# Revit family: Shower-Kohler-Devonshire-T396_4X
name_source: partatom
category: Plumbing Fixtures
revit_build: Autodesk Revit MEP 2012 (Build: 20110916_2132(x64)
units: mm (PartAtom-declared; Revit-internal decimal feet)

## types (6) — shared parameters
Date Modified = January 26, 2015
Default Elevation = 48 "
Description = See Part Description
Equipment Abbreviation = SW
Family Version = 1.0
Manufacturer = Kohler Company
Model = See Part Number
Model Disclaimer = Contact Kohler Company For More Information
Product Page URL = http://www.us.kohler.com
Shower Head Connection Radius = 0.25 "
URL = http://www.us.kohler.com
zz Length 3 = 7 "
zz Length 5 = 7 "

## per-type parameters (varying)
| type | Product Material | zz Integer 1 |
| Oil Rubbed Bronze | Metal - Kohler - Oil Rubbed Bronze | 6 |
| Vibrant Brushed Bronze | Metal - Kohler - Vibrant Brushed Bronze | 5 |
| Vibrant Brushed Nickel | Metal - Kohler - Vibrant Brushed Nickel | 4 |
| Vibrant Polished Brass | Metal - Kohler - Vibrant Polished Brass | 3 |
| Vibrant Polished Nickel | Metal - Kohler - Vibrant Polished Nickel | 2 |
| Polished Chrome | Chrome - Kohler - Polished | 1 |

## geometry (parser evidence)
native form markers: Sweep x2
no freeform markers — native parametric forms only
